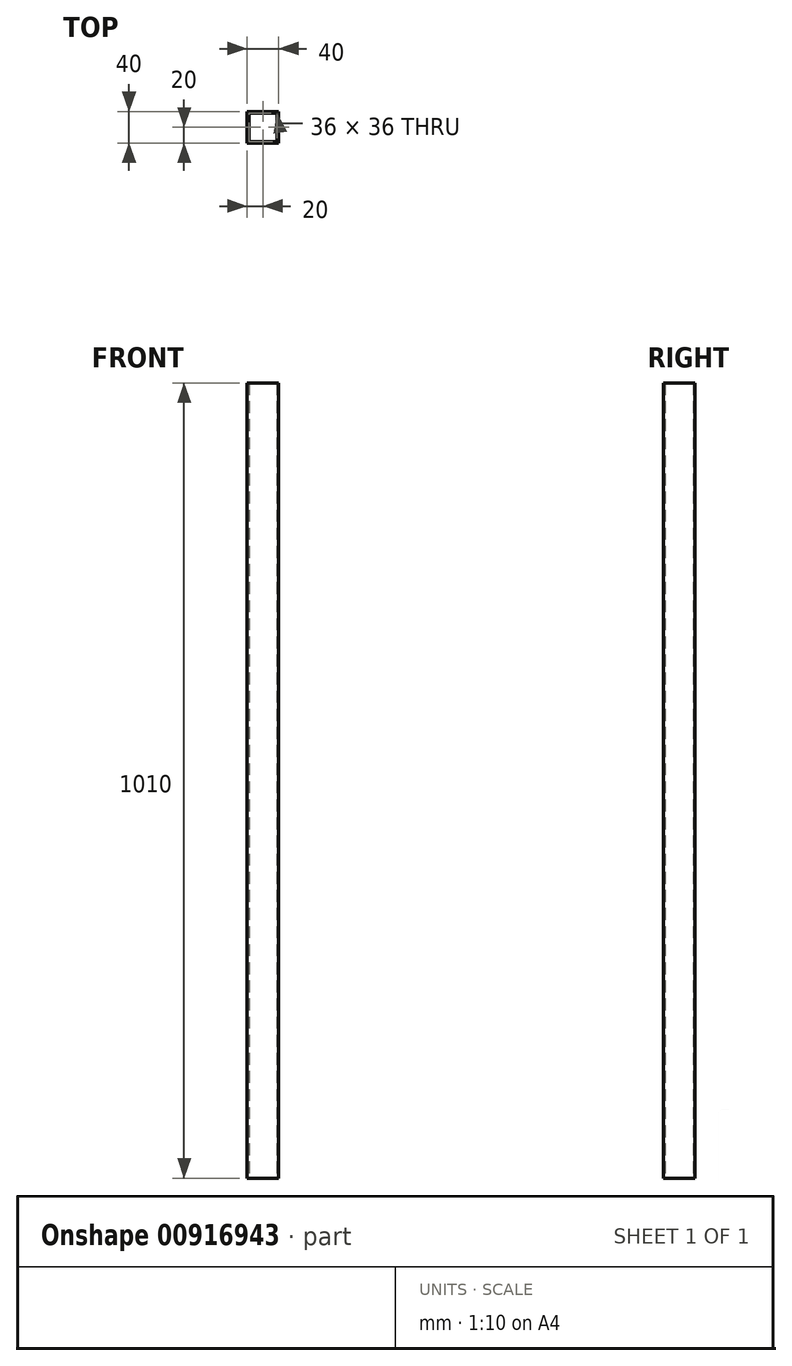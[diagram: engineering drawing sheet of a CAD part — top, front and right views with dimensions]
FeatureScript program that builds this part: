
annotation { "Feature Type Name" : "Feature", "Feature Type Description" : "" }
export const myFeature = defineFeature(function(context is Context, id is Id, definition is map)
    precondition{}
    {
        {
            var Q0;
            Q0=qCreatedBy(makeId("Top.planeOp"),FACE);
            var sketch = newSketch(context, id + "F0", { "sketchPlane" : qUnion([Q0])});
            skLineSegment(sketch, "E0.bottom", {"start": v(0, 0) * mm, "end": v(40, 0) * mm});
            skLineSegment(sketch, "E0.top", {"start": v(0, 40) * mm, "end": v(40, 40) * mm});
            skLineSegment(sketch, "E0.left", {"start": v(0, 0) * mm, "end": v(0, 40) * mm});
            skLineSegment(sketch, "E0.right", {"start": v(40, 0) * mm, "end": v(40, 40) * mm});
            skLineSegment(sketch, "E1.0", {"start": v(2, 2) * mm, "end": v(38, 2) * mm});
            skLineSegment(sketch, "E1.1", {"start": v(2, 2) * mm, "end": v(2, 38) * mm});
            skLineSegment(sketch, "E1.2", {"start": v(2, 38) * mm, "end": v(38, 38) * mm});
            skLineSegment(sketch, "E1.3", {"start": v(38, 2) * mm, "end": v(38, 38) * mm});
            skSolve(sketch);
        }
        {
            var Q0;
            Q0=makeQuery(id+"F0.imprint","IMPRINT",FACE,{"disambiguationData":[TD([[makeQuery(id+"F0.imprint","IMPRINT",EDGE,{"derivedFrom":sQuery(id+"F0.wireOp",EDGE,"E0.bottom")}),1.0]])]});
            extrude(context, id + "F1", {"entities" : qUnion([Q0]), "depth" : 1010 * mm, "offsetDistance" : 25 * mm});
        }
    });
